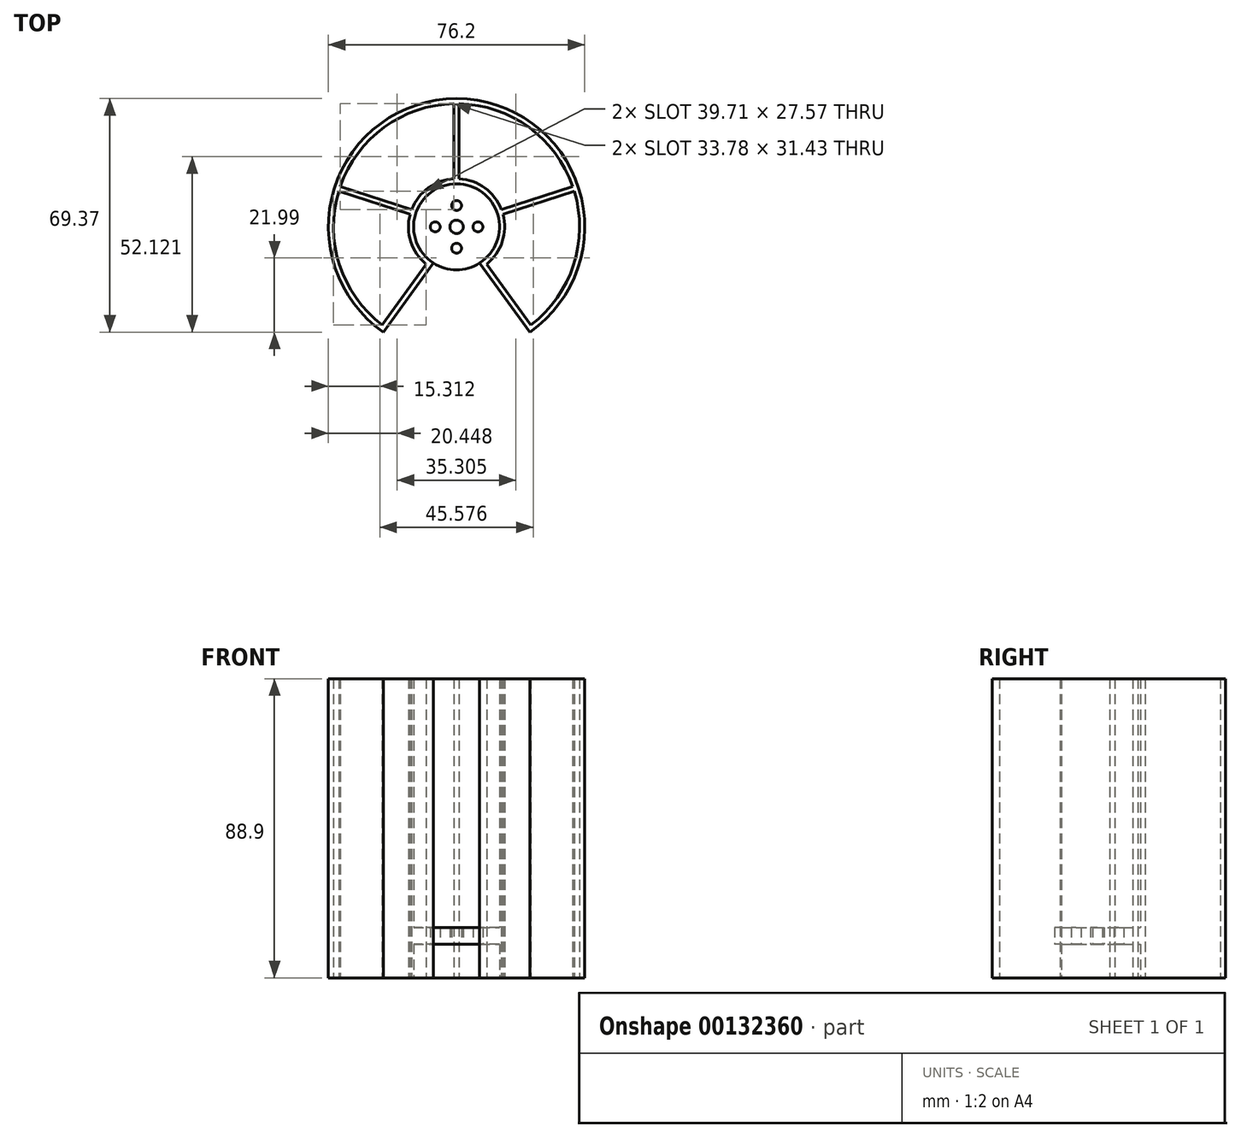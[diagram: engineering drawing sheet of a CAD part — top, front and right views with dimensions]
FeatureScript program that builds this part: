
annotation { "Feature Type Name" : "Feature", "Feature Type Description" : "" }
export const myFeature = defineFeature(function(context is Context, id is Id, definition is map)
    precondition{}
    {
        {
            var Q0;
            Q0=qCreatedBy(makeId("Top.planeOp"),FACE);
            var sketch = newSketch(context, id + "F0", { "sketchPlane" : qUnion([Q0])});
            skCircle(sketch, "E0", {"center": v(0, 0) * mm, "radius": 38.1 * mm});
            skCircle(sketch, "E1", {"center": v(0, 0) * mm, "radius": 14.29 * mm});
            skCircle(sketch, "E2.0", {"center": v(0, 0) * mm, "radius": 12.76 * mm});
            skCircle(sketch, "E3.0", {"center": v(0, 0) * mm, "radius": 36.58 * mm});
            skLineSegment(sketch, "E4", {"start": v(0, 36.58) * mm, "end": v(0, 14.29) * mm});
            skLineSegment(sketch, "E5", {"start": v(-0.76, 14.27) * mm, "end": v(-0.76, 36.57) * mm});
            skLineSegment(sketch, "E6", {"start": v(0.76, 36.57) * mm, "end": v(0.76, 14.27) * mm});
            skLineSegment(sketch, "E7.1.0", {"start": v(-13.8, 3.68) * mm, "end": v(-35.01, 10.58) * mm});
            skLineSegment(sketch, "E7.1.1", {"start": v(-34.79, 11.3) * mm, "end": v(-13.59, 4.42) * mm});
            skLineSegment(sketch, "E7.1.2", {"start": v(-34.54, 12.02) * mm, "end": v(-13.33, 5.13) * mm});
            skLineSegment(sketch, "E7.2.0", {"start": v(-7.77, -12) * mm, "end": v(-20.88, -30.03) * mm});
            skLineSegment(sketch, "E7.2.1", {"start": v(-21.5, -29.6) * mm, "end": v(-8.4, -11.56) * mm});
            skLineSegment(sketch, "E7.2.2", {"start": v(-22.11, -29.14) * mm, "end": v(-9, -11.1) * mm});
            skLineSegment(sketch, "E7.3.0", {"start": v(9, -11.1) * mm, "end": v(22.11, -29.14) * mm});
            skLineSegment(sketch, "E7.3.1", {"start": v(21.5, -29.6) * mm, "end": v(8.4, -11.56) * mm});
            skLineSegment(sketch, "E7.3.2", {"start": v(20.88, -30.03) * mm, "end": v(7.77, -12) * mm});
            skLineSegment(sketch, "E7.4.0", {"start": v(13.33, 5.13) * mm, "end": v(34.54, 12.02) * mm});
            skLineSegment(sketch, "E7.4.1", {"start": v(34.79, 11.3) * mm, "end": v(13.59, 4.42) * mm});
            skLineSegment(sketch, "E7.4.2", {"start": v(35.01, 10.58) * mm, "end": v(13.8, 3.68) * mm});
            skLineSegment(sketch, "E8", {"start": v(0, 0) * mm, "end": v(0, 6.35) * mm});
            skLineSegment(sketch, "E9.1.0", {"start": v(0, 0) * mm, "end": v(-6.35, 0) * mm});
            skLineSegment(sketch, "E9.2.0", {"start": v(0, 0) * mm, "end": v(0, -6.35) * mm});
            skLineSegment(sketch, "E9.3.0", {"start": v(0, 0) * mm, "end": v(6.35, 0) * mm});
            skLineSegment(sketch, "E10", {"start": v(7.77, -12) * mm, "end": v(6.87, -10.76) * mm});
            skLineSegment(sketch, "E11", {"start": v(-7.77, -12) * mm, "end": v(-6.87, -10.76) * mm});
            skLineSegment(sketch, "E12", {"start": v(-20.88, -30.03) * mm, "end": v(-21.77, -31.27) * mm});
            skLineSegment(sketch, "E13", {"start": v(20.88, -30.03) * mm, "end": v(21.77, -31.27) * mm});
            skSolve(sketch);
        }
        {
            var Q0;
            {var subQ3=sQuery(id+"F0.wireOp",EDGE,"E10");Q0=makeQuery(id+"F0.imprint","IMPRINT",FACE,{"disambiguationData":[TD([[makeQuery(id+"F0.imprint","IMPRINT",EDGE,{"derivedFrom":subQ3}),-1.0]])]});}
            var Q1;
            {var subQ0=sQuery(id+"F0.wireOp",EDGE,"E4");Q1=makeQuery(id+"F0.imprint","IMPRINT",FACE,{"disambiguationData":[TD([[makeQuery(id+"F0.imprint","IMPRINT",EDGE,{"derivedFrom":subQ0}),-1.0]])]});}
            var Q2;
            {var subQ0=sQuery(id+"F0.wireOp",EDGE,"E4");Q2=makeQuery(id+"F0.imprint","IMPRINT",FACE,{"disambiguationData":[TD([[makeQuery(id+"F0.imprint","IMPRINT",EDGE,{"derivedFrom":subQ0}),1.0]])]});}
            var Q3;
            {var subQ0=sQuery(id+"F0.wireOp",EDGE,"E7.4.0");Q3=makeQuery(id+"F0.imprint","IMPRINT",FACE,{"disambiguationData":[TD([[makeQuery(id+"F0.imprint","IMPRINT",EDGE,{"derivedFrom":subQ0}),-1.0]])]});}
            var Q4;
            {var subQ0=sQuery(id+"F0.wireOp",EDGE,"E7.4.1");Q4=makeQuery(id+"F0.imprint","IMPRINT",FACE,{"disambiguationData":[TD([[makeQuery(id+"F0.imprint","IMPRINT",EDGE,{"derivedFrom":subQ0}),1.0]])]});}
            var Q5;
            {var subQ0=sQuery(id+"F0.wireOp",EDGE,"E7.1.1");Q5=makeQuery(id+"F0.imprint","IMPRINT",FACE,{"disambiguationData":[TD([[makeQuery(id+"F0.imprint","IMPRINT",EDGE,{"derivedFrom":subQ0}),1.0]])]});}
            var Q6;
            {var subQ0=sQuery(id+"F0.wireOp",EDGE,"E7.1.0");Q6=makeQuery(id+"F0.imprint","IMPRINT",FACE,{"disambiguationData":[TD([[makeQuery(id+"F0.imprint","IMPRINT",EDGE,{"derivedFrom":subQ0}),-1.0]])]});}
            var Q7;
            {var subQ14=sQuery(id+"F0.wireOp",EDGE,"E12");Q7=makeQuery(id+"F0.imprint","IMPRINT",FACE,{"disambiguationData":[TD([[makeQuery(id+"F0.imprint","IMPRINT",EDGE,{"derivedFrom":subQ14}),-1.0]])]});}
            var Q8;
            {var subQ0=sQuery(id+"F0.wireOp",EDGE,"E7.3.1");Q8=makeQuery(id+"F0.imprint","IMPRINT",FACE,{"disambiguationData":[TD([[makeQuery(id+"F0.imprint","IMPRINT",EDGE,{"derivedFrom":subQ0}),1.0]])]});}
            var Q9;
            {var subQ0=sQuery(id+"F0.wireOp",EDGE,"E7.3.0");Q9=makeQuery(id+"F0.imprint","IMPRINT",FACE,{"disambiguationData":[TD([[makeQuery(id+"F0.imprint","IMPRINT",EDGE,{"derivedFrom":subQ0}),-1.0]])]});}
            var Q10;
            {var subQ0=sQuery(id+"F0.wireOp",EDGE,"E7.2.0");Q10=makeQuery(id+"F0.imprint","IMPRINT",FACE,{"disambiguationData":[TD([[makeQuery(id+"F0.imprint","IMPRINT",EDGE,{"derivedFrom":subQ0}),-1.0]])]});}
            var Q11;
            {var subQ0=sQuery(id+"F0.wireOp",EDGE,"E7.2.1");Q11=makeQuery(id+"F0.imprint","IMPRINT",FACE,{"disambiguationData":[TD([[makeQuery(id+"F0.imprint","IMPRINT",EDGE,{"derivedFrom":subQ0}),1.0]])]});}
            extrude(context, id + "F1", {"entities" : qUnion([Q0, Q1, Q2, Q3, Q4, Q5, Q6, Q7, Q8, Q9, Q10, Q11]), "depth" : 88.9 * mm});
        }
        {
            var Q0;
            Q0=qCreatedBy(makeId("Top.planeOp"),FACE);
            cPlane(context, id + "F2", {"entities" : qUnion([Q0]), "cplaneType" : CPlaneType.OFFSET, "offset" : 10 * mm, "width" : 152.4 * mm, "height" : 152.4 * mm});
        }
        {
            var Q0;
            Q0=qCreatedBy(id+"F2.planeOp",FACE);
            var sketch = newSketch(context, id + "F3", { "sketchPlane" : qUnion([Q0])});
            skCircle(sketch, "E14", {"center": v(0, 0) * mm, "radius": 12.76 * mm});
            skLineSegment(sketch, "E15", {"start": v(0, 0) * mm, "end": v(0, 6.35) * mm});
            skLineSegment(sketch, "E16.1.0", {"start": v(0, 0) * mm, "end": v(-6.35, 0) * mm});
            skLineSegment(sketch, "E16.2.0", {"start": v(0, 0) * mm, "end": v(0, -6.35) * mm});
            skLineSegment(sketch, "E16.3.0", {"start": v(0, 0) * mm, "end": v(6.35, 0) * mm});
            skSolve(sketch);
        }
        {
            var Q0;
            Q0=makeQuery(id+"F3.imprint","IMPRINT",FACE,{"disambiguationData":[TD([[makeQuery(id+"F3.imprint","IMPRINT",EDGE,{"derivedFrom":sQuery(id+"F3.wireOp",EDGE,"E14")}),1.0]])]});
            extrude(context, id + "F4", {"entities" : qUnion([Q0]), "operationType" : NewBodyOperationType.ADD, "depth" : 5 * mm});
        }
        {
            var Q0;
            Q0=sQuery(id+"F3.wireOp",VERTEX,"E15.end");
            var Q1;
            Q1=sQuery(id+"F3.wireOp",VERTEX,"E16.3.0.end");
            var Q2;
            Q2=sQuery(id+"F3.wireOp",VERTEX,"E16.2.0.end");
            var Q3;
            Q3=sQuery(id+"F3.wireOp",VERTEX,"E16.1.0.end");
            var Q4;
            Q4=makeQuery(id+"F1.opExtrude","SWEPT_BODY",BODY,{"disambiguationData":[OSD([sQuery(id+"F0.wireOp",EDGE,"E0"),sQuery(id+"F0.wireOp",EDGE,"E1"),sQuery(id+"F0.wireOp",EDGE,"E2.0"),sQuery(id+"F0.wireOp",EDGE,"E3.0"),sQuery(id+"F0.wireOp",EDGE,"E5"),sQuery(id+"F0.wireOp",EDGE,"E6"),sQuery(id+"F0.wireOp",EDGE,"E7.1.0"),sQuery(id+"F0.wireOp",EDGE,"E7.1.2"),sQuery(id+"F0.wireOp",EDGE,"E7.2.0"),sQuery(id+"F0.wireOp",EDGE,"E7.2.2"),sQuery(id+"F0.wireOp",EDGE,"E7.3.0"),sQuery(id+"F0.wireOp",EDGE,"E7.3.2"),sQuery(id+"F0.wireOp",EDGE,"E7.4.0"),sQuery(id+"F0.wireOp",EDGE,"E7.4.2"),sQuery(id+"F0.wireOp",EDGE,"E10"),sQuery(id+"F0.wireOp",EDGE,"E11"),sQuery(id+"F0.wireOp",EDGE,"E12"),sQuery(id+"F0.wireOp",EDGE,"E13")])]});
            hole(context, id + "F5", {"style" : HoleStyle.SIMPLE, "endStyle" : HoleEndStyle.THROUGH, "oppositeDirection" : true, "standardTappedOrClearance" : lookupTablePath({ "standard" : "ANSI", "fit" : "Close", "size" : "#4", "type" : "Clearance" }), "standardBlindInLast" : lookupTablePath({ "fit" : "Close", "standard" : "ANSI", "size" : "#4", "type" : "Clearance" }), "holeDiameter" : 2.95 * mm, "locations" : qUnion([Q0, Q1, Q2, Q3]), "scope" : qUnion([Q4]), "isTappedThrough" : true});
        }
        {
            var Q0;
            Q0=sQuery(id+"F3.wireOp",VERTEX,"E14.center");
            var Q1;
            Q1=makeQuery(id+"F1.opExtrude","SWEPT_BODY",BODY,{"disambiguationData":[OSD([sQuery(id+"F0.wireOp",EDGE,"E0"),sQuery(id+"F0.wireOp",EDGE,"E1"),sQuery(id+"F0.wireOp",EDGE,"E2.0"),sQuery(id+"F0.wireOp",EDGE,"E3.0"),sQuery(id+"F0.wireOp",EDGE,"E5"),sQuery(id+"F0.wireOp",EDGE,"E6"),sQuery(id+"F0.wireOp",EDGE,"E7.1.0"),sQuery(id+"F0.wireOp",EDGE,"E7.1.2"),sQuery(id+"F0.wireOp",EDGE,"E7.2.0"),sQuery(id+"F0.wireOp",EDGE,"E7.2.2"),sQuery(id+"F0.wireOp",EDGE,"E7.3.0"),sQuery(id+"F0.wireOp",EDGE,"E7.3.2"),sQuery(id+"F0.wireOp",EDGE,"E7.4.0"),sQuery(id+"F0.wireOp",EDGE,"E7.4.2"),sQuery(id+"F0.wireOp",EDGE,"E10"),sQuery(id+"F0.wireOp",EDGE,"E11"),sQuery(id+"F0.wireOp",EDGE,"E12"),sQuery(id+"F0.wireOp",EDGE,"E13")])]});
            hole(context, id + "F6", {"style" : HoleStyle.SIMPLE, "endStyle" : HoleEndStyle.THROUGH, "oppositeDirection" : true, "holeDiameter" : 4 * mm, "locations" : qUnion([Q0]), "scope" : qUnion([Q1]), "isTappedThrough" : true});
        }
    });
